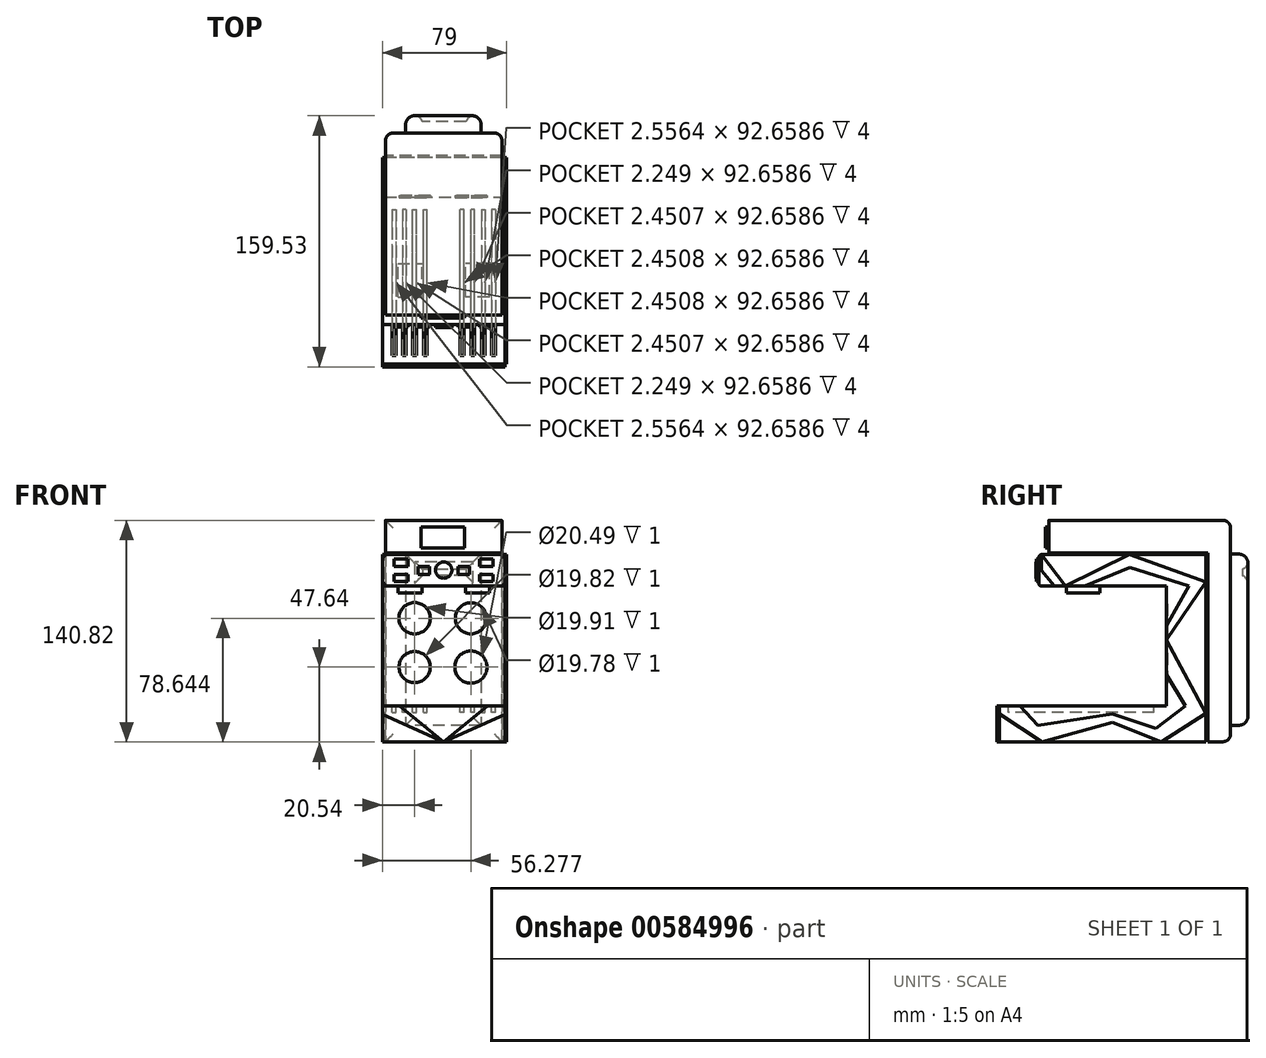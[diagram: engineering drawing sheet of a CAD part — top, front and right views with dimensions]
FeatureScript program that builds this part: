
annotation { "Feature Type Name" : "Feature", "Feature Type Description" : "" }
export const myFeature = defineFeature(function(context is Context, id is Id, definition is map)
    precondition{}
    {
        {
            var Q0;
            Q0=qCreatedBy(makeId("Right.planeOp"),FACE);
            var sketch = newSketch(context, id + "F0", { "sketchPlane" : qUnion([Q0])});
            skLineSegment(sketch, "E0", {"start": v(-54.68, 43.8) * mm, "end": v(-54.68, 23.88) * mm});
            skLineSegment(sketch, "E1", {"start": v(-54.68, 23.88) * mm, "end": v(27.35, 23.88) * mm});
            skLineSegment(sketch, "E2", {"start": v(27.35, 23.88) * mm, "end": v(27.35, -53.5) * mm});
            skLineSegment(sketch, "E3", {"start": v(27.35, -53.5) * mm, "end": v(-73.32, -53.5) * mm});
            skLineSegment(sketch, "E4", {"start": v(-73.32, -53.5) * mm, "end": v(-73.32, -74.72) * mm});
            skLineSegment(sketch, "E5", {"start": v(-73.32, -74.72) * mm, "end": v(48.83, -74.72) * mm});
            skLineSegment(sketch, "E6", {"start": v(48.83, -74.72) * mm, "end": v(48.83, 43.8) * mm});
            skLineSegment(sketch, "E7", {"start": v(48.83, 43.8) * mm, "end": v(-54.68, 43.8) * mm});
            skLineSegment(sketch, "E8", {"start": v(-46.66, 43.8) * mm, "end": v(-46.66, 64.76) * mm});
            skLineSegment(sketch, "E9", {"start": v(-46.66, 64.76) * mm, "end": v(69.53, 64.76) * mm});
            skLineSegment(sketch, "E10", {"start": v(69.53, 64.76) * mm, "end": v(69.53, -74.72) * mm});
            skLineSegment(sketch, "E11", {"start": v(48.83, -74.72) * mm, "end": v(69.53, -74.72) * mm});
            skPoint(sketch, "E12.orphan", {"position": v(69.53, -76.01) * mm});
            skSolve(sketch);
        }
        {
            var Q0;
            {var subQ0=sQuery(id+"F0.wireOp",EDGE,"E0");Q0=makeQuery(id+"F0.imprint","IMPRINT",FACE,{"disambiguationData":[TD([[makeQuery(id+"F0.imprint","IMPRINT",EDGE,{"derivedFrom":subQ0}),1.0]])]});}
            var Q1;
            {var subQ2=sQuery(id+"F0.wireOp",EDGE,"E6");Q1=makeQuery(id+"F0.imprint","IMPRINT",FACE,{"disambiguationData":[TD([[makeQuery(id+"F0.imprint","IMPRINT",EDGE,{"derivedFrom":subQ2}),-1.0]])]});}
            extrude(context, id + "F1", {"entities" : qUnion([Q0, Q1]), "depth" : 82 * mm, "offsetDistance" : 25 * mm, "symmetric" : true});
        }
        {
            var Q0;
            Q0=makeQuery(id+"F1.opExtrude","CAP_FACE",FACE,{"disambiguationData":[OSD([sQuery(id+"F0.wireOp",EDGE,"E0"),sQuery(id+"F0.wireOp",EDGE,"E1"),sQuery(id+"F0.wireOp",EDGE,"E2"),sQuery(id+"F0.wireOp",EDGE,"E3"),sQuery(id+"F0.wireOp",EDGE,"E4"),sQuery(id+"F0.wireOp",EDGE,"E5"),sQuery(id+"F0.wireOp",EDGE,"E7"),sQuery(id+"F0.wireOp",EDGE,"E8"),sQuery(id+"F0.wireOp",EDGE,"E9"),sQuery(id+"F0.wireOp",EDGE,"E10"),sQuery(id+"F0.wireOp",EDGE,"E11")])],"isStart":false});
            extrude(context, id + "F2", {"entities" : qUnion([Q0]), "operationType" : NewBodyOperationType.ADD, "depth" : 15 * mm, "offsetDistance" : 25 * mm});
        }
        {
            var Q0;
            Q0=makeQuery(id+"F1.opExtrude","SWEPT_BODY",BODY,{"disambiguationData":[OSD([sQuery(id+"F0.wireOp",EDGE,"E0"),sQuery(id+"F0.wireOp",EDGE,"E1"),sQuery(id+"F0.wireOp",EDGE,"E2"),sQuery(id+"F0.wireOp",EDGE,"E3"),sQuery(id+"F0.wireOp",EDGE,"E4"),sQuery(id+"F0.wireOp",EDGE,"E5"),sQuery(id+"F0.wireOp",EDGE,"E7"),sQuery(id+"F0.wireOp",EDGE,"E8"),sQuery(id+"F0.wireOp",EDGE,"E9"),sQuery(id+"F0.wireOp",EDGE,"E10"),sQuery(id+"F0.wireOp",EDGE,"E11")])]});
            deleteBodies(context, id + "F3", {"entities" : qUnion([Q0])});
        }
        {
            var Q0;
            Q0=qCreatedBy(makeId("Right.planeOp"),FACE);
            var sketch = newSketch(context, id + "F4", { "sketchPlane" : qUnion([Q0])});
            skLineSegment(sketch, "E13", {"start": v(-46.6, 54.07) * mm, "end": v(-46.6, 34.04) * mm});
            skLineSegment(sketch, "E14", {"start": v(-46.6, 34.04) * mm, "end": v(34.23, 34.04) * mm});
            skLineSegment(sketch, "E15", {"start": v(34.23, 34.04) * mm, "end": v(34.23, -42.06) * mm});
            skLineSegment(sketch, "E16", {"start": v(34.23, -42.06) * mm, "end": v(-71.74, -42.06) * mm});
            skLineSegment(sketch, "E17", {"start": v(-71.74, -42.06) * mm, "end": v(-71.74, -65) * mm});
            skLineSegment(sketch, "E18", {"start": v(-71.74, -65) * mm, "end": v(59.35, -65) * mm});
            skLineSegment(sketch, "E19", {"start": v(59.35, -65) * mm, "end": v(59.35, 54.07) * mm});
            skLineSegment(sketch, "E20", {"start": v(59.35, 54.07) * mm, "end": v(-46.6, 54.07) * mm});
            skSolve(sketch);
        }
        {
            var Q0;
            Q0=makeQuery(id+"F4.imprint","IMPRINT",FACE,{"disambiguationData":[TD([[makeQuery(id+"F4.imprint","IMPRINT",EDGE,{"derivedFrom":sQuery(id+"F4.wireOp",EDGE,"E13")}),1.0]])]});
            extrude(context, id + "F5", {"entities" : qUnion([Q0]), "depth" : 78 * mm, "offsetDistance" : 25 * mm, "symmetric" : true});
        }
        {
            var Q0;
            Q0=qCreatedBy(makeId("Right.planeOp"),FACE);
            var sketch = newSketch(context, id + "F6", { "sketchPlane" : qUnion([Q0])});
            skLineSegment(sketch, "E21", {"start": v(-40.38, 55.14) * mm, "end": v(60.81, 55.14) * mm});
            skLineSegment(sketch, "E22", {"start": v(60.81, 55.14) * mm, "end": v(60.81, -64.77) * mm});
            skLineSegment(sketch, "E23", {"start": v(60.81, -64.77) * mm, "end": v(75.1, -64.77) * mm});
            skLineSegment(sketch, "E24", {"start": v(75.1, -64.77) * mm, "end": v(75.1, 75.82) * mm});
            skLineSegment(sketch, "E25", {"start": v(75.1, 75.82) * mm, "end": v(-40.38, 75.82) * mm});
            skLineSegment(sketch, "E26", {"start": v(-40.38, 75.82) * mm, "end": v(-40.38, 55.14) * mm});
            skSolve(sketch);
        }
        {
            var Q0;
            Q0=makeQuery(id+"F6.imprint","IMPRINT",FACE,{"disambiguationData":[TD([[makeQuery(id+"F6.imprint","IMPRINT",EDGE,{"derivedFrom":sQuery(id+"F6.wireOp",EDGE,"E21")}),1.0]])]});
            extrude(context, id + "F7", {"entities" : qUnion([Q0]), "depth" : 74 * mm, "offsetDistance" : 25 * mm, "symmetric" : true});
        }
        {
            var Q0;
            Q0=makeQuery(id+"F5.opExtrude","SWEPT_FACE",FACE,{"disambiguationData":[OSD([sQuery(id+"F4.wireOp",EDGE,"E16")])]});
            var sketch = newSketch(context, id + "F8", { "sketchPlane" : qUnion([Q0])});
            skLineSegment(sketch, "E27.bottom", {"start": v(-32.9, 26.57) * mm, "end": v(-30.35, 26.57) * mm});
            skLineSegment(sketch, "E27.top", {"start": v(-32.9, -66.09) * mm, "end": v(-30.35, -66.09) * mm});
            skLineSegment(sketch, "E27.left", {"start": v(-32.9, 26.57) * mm, "end": v(-32.9, -66.09) * mm});
            skLineSegment(sketch, "E27.right", {"start": v(-30.35, 26.57) * mm, "end": v(-30.35, -66.09) * mm});
            skLineSegment(sketch, "E28.bottom", {"start": v(-23.97, 26.57) * mm, "end": v(-26.22, 26.57) * mm});
            skLineSegment(sketch, "E28.top", {"start": v(-23.97, -66.09) * mm, "end": v(-26.22, -66.09) * mm});
            skLineSegment(sketch, "E28.left", {"start": v(-23.97, 26.57) * mm, "end": v(-23.97, -66.09) * mm});
            skLineSegment(sketch, "E28.right", {"start": v(-26.22, 26.57) * mm, "end": v(-26.22, -66.09) * mm});
            skLineSegment(sketch, "E29.bottom", {"start": v(-19.69, -66.09) * mm, "end": v(-17.24, -66.09) * mm});
            skLineSegment(sketch, "E29.top", {"start": v(-19.69, 26.57) * mm, "end": v(-17.24, 26.57) * mm});
            skLineSegment(sketch, "E29.left", {"start": v(-19.69, -66.09) * mm, "end": v(-19.69, 26.57) * mm});
            skLineSegment(sketch, "E29.right", {"start": v(-17.24, -66.09) * mm, "end": v(-17.24, 26.57) * mm});
            skLineSegment(sketch, "E30.bottom", {"start": v(-12.9, -66.09) * mm, "end": v(-10.45, -66.09) * mm});
            skLineSegment(sketch, "E30.top", {"start": v(-12.9, 26.57) * mm, "end": v(-10.45, 26.57) * mm});
            skLineSegment(sketch, "E30.left", {"start": v(-12.9, -66.09) * mm, "end": v(-12.9, 26.57) * mm});
            skLineSegment(sketch, "E30.right", {"start": v(-10.45, -66.09) * mm, "end": v(-10.45, 26.57) * mm});
            skLineSegment(sketch, "E31.MirrorCS", {"start": v(12.9, -66.09) * mm, "end": v(12.9, 26.57) * mm});
            skLineSegment(sketch, "E32.MirrorCS", {"start": v(10.45, -66.09) * mm, "end": v(10.45, 26.57) * mm});
            skLineSegment(sketch, "E33.MirrorCS", {"start": v(17.24, -66.09) * mm, "end": v(17.24, 26.57) * mm});
            skLineSegment(sketch, "E34.MirrorCS", {"start": v(19.69, -66.09) * mm, "end": v(19.69, 26.57) * mm});
            skLineSegment(sketch, "E35.MirrorCS", {"start": v(26.22, 26.57) * mm, "end": v(26.22, -66.09) * mm});
            skLineSegment(sketch, "E36.MirrorCS", {"start": v(23.97, 26.57) * mm, "end": v(23.97, -66.09) * mm});
            skLineSegment(sketch, "E37.MirrorCS", {"start": v(32.9, 26.57) * mm, "end": v(32.9, -66.09) * mm});
            skLineSegment(sketch, "E38.MirrorCS", {"start": v(30.35, 26.57) * mm, "end": v(30.35, -66.09) * mm});
            skLineSegment(sketch, "E39.MirrorCS", {"start": v(32.9, 26.57) * mm, "end": v(30.35, 26.57) * mm});
            skLineSegment(sketch, "E40.MirrorCS", {"start": v(23.97, 26.57) * mm, "end": v(26.22, 26.57) * mm});
            skLineSegment(sketch, "E41.MirrorCS", {"start": v(19.69, 26.57) * mm, "end": v(17.24, 26.57) * mm});
            skLineSegment(sketch, "E42.MirrorCS", {"start": v(12.9, 26.57) * mm, "end": v(10.45, 26.57) * mm});
            skLineSegment(sketch, "E43.MirrorCS", {"start": v(32.9, -66.09) * mm, "end": v(30.35, -66.09) * mm});
            skLineSegment(sketch, "E44.MirrorCS", {"start": v(23.97, -66.09) * mm, "end": v(26.22, -66.09) * mm});
            skLineSegment(sketch, "E45.MirrorCS", {"start": v(19.69, -66.09) * mm, "end": v(17.24, -66.09) * mm});
            skLineSegment(sketch, "E46.MirrorCS", {"start": v(12.9, -66.09) * mm, "end": v(10.45, -66.09) * mm});
            skSolve(sketch);
        }
        {
            var Q0;
            Q0=makeQuery(id+"F8.imprint","IMPRINT",FACE,{"disambiguationData":[TD([[makeQuery(id+"F8.imprint","IMPRINT",EDGE,{"derivedFrom":sQuery(id+"F8.wireOp",EDGE,"E27.bottom")}),-1.0]])]});
            var Q1;
            Q1=makeQuery(id+"F8.imprint","IMPRINT",FACE,{"disambiguationData":[TD([[makeQuery(id+"F8.imprint","IMPRINT",EDGE,{"derivedFrom":sQuery(id+"F8.wireOp",EDGE,"E28.bottom")}),1.0]])]});
            var Q2;
            Q2=makeQuery(id+"F8.imprint","IMPRINT",FACE,{"disambiguationData":[TD([[makeQuery(id+"F8.imprint","IMPRINT",EDGE,{"derivedFrom":sQuery(id+"F8.wireOp",EDGE,"E29.bottom")}),1.0]])]});
            var Q3;
            Q3=makeQuery(id+"F8.imprint","IMPRINT",FACE,{"disambiguationData":[TD([[makeQuery(id+"F8.imprint","IMPRINT",EDGE,{"derivedFrom":sQuery(id+"F8.wireOp",EDGE,"E30.bottom")}),1.0]])]});
            var Q4;
            Q4=makeQuery(id+"F8.imprint","IMPRINT",FACE,{"disambiguationData":[TD([[makeQuery(id+"F8.imprint","IMPRINT",EDGE,{"derivedFrom":sQuery(id+"F8.wireOp",EDGE,"E31.MirrorCS")}),1.0]])]});
            var Q5;
            Q5=makeQuery(id+"F8.imprint","IMPRINT",FACE,{"disambiguationData":[TD([[makeQuery(id+"F8.imprint","IMPRINT",EDGE,{"derivedFrom":sQuery(id+"F8.wireOp",EDGE,"E33.MirrorCS")}),-1.0]])]});
            var Q6;
            Q6=makeQuery(id+"F8.imprint","IMPRINT",FACE,{"disambiguationData":[TD([[makeQuery(id+"F8.imprint","IMPRINT",EDGE,{"derivedFrom":sQuery(id+"F8.wireOp",EDGE,"E35.MirrorCS")}),-1.0]])]});
            var Q7;
            Q7=makeQuery(id+"F8.imprint","IMPRINT",FACE,{"disambiguationData":[TD([[makeQuery(id+"F8.imprint","IMPRINT",EDGE,{"derivedFrom":sQuery(id+"F8.wireOp",EDGE,"E37.MirrorCS")}),-1.0]])]});
            extrude(context, id + "F9", {"entities" : qUnion([Q0, Q1, Q2, Q3, Q4, Q5, Q6, Q7]), "operationType" : NewBodyOperationType.REMOVE, "oppositeDirection" : true, "depth" : 4 * mm, "offsetDistance" : 25 * mm});
        }
        {
            var Q0;
            Q0=makeQuery(id+"F5.opExtrude","SWEPT_FACE",FACE,{"disambiguationData":[OSD([sQuery(id+"F4.wireOp",EDGE,"E14")])]});
            var sketch = newSketch(context, id + "F10", { "sketchPlane" : qUnion([Q0])});
            skLineSegment(sketch, "E47.bottom", {"start": v(-29.04, 29.07) * mm, "end": v(-13.9, 29.07) * mm});
            skLineSegment(sketch, "E47.top", {"start": v(-29.04, 7.88) * mm, "end": v(-13.9, 7.88) * mm});
            skLineSegment(sketch, "E47.left", {"start": v(-29.04, 29.07) * mm, "end": v(-29.04, 7.88) * mm});
            skLineSegment(sketch, "E47.right", {"start": v(-13.9, 29.07) * mm, "end": v(-13.9, 7.88) * mm});
            skLineSegment(sketch, "E48.MirrorCS", {"start": v(13.9, 29.07) * mm, "end": v(13.9, 7.88) * mm});
            skLineSegment(sketch, "E49.MirrorCS", {"start": v(29.04, 29.07) * mm, "end": v(13.9, 29.07) * mm});
            skLineSegment(sketch, "E50.MirrorCS", {"start": v(29.04, 29.07) * mm, "end": v(29.04, 7.88) * mm});
            skLineSegment(sketch, "E51.MirrorCS", {"start": v(29.04, 7.88) * mm, "end": v(13.9, 7.88) * mm});
            skSolve(sketch);
        }
        {
            var Q0;
            Q0=makeQuery(id+"F10.imprint","IMPRINT",FACE,{"disambiguationData":[TD([[makeQuery(id+"F10.imprint","IMPRINT",EDGE,{"derivedFrom":sQuery(id+"F10.wireOp",EDGE,"E47.bottom")}),-1.0]])]});
            var Q1;
            Q1=makeQuery(id+"F10.imprint","IMPRINT",FACE,{"disambiguationData":[TD([[makeQuery(id+"F10.imprint","IMPRINT",EDGE,{"derivedFrom":sQuery(id+"F10.wireOp",EDGE,"E48.MirrorCS")}),1.0]])]});
            extrude(context, id + "F11", {"entities" : qUnion([Q0, Q1]), "depth" : 4.2 * mm, "offsetDistance" : 25 * mm});
        }
        {
            var Q0;
            Q0=makeQuery(id+"F7.opExtrude","SWEPT_FACE",FACE,{"disambiguationData":[OSD([sQuery(id+"F6.wireOp",EDGE,"E26")])]});
            var sketch = newSketch(context, id + "F12", { "sketchPlane" : qUnion([Q0])});
            skLineSegment(sketch, "E52.bottom", {"start": v(-14.42, 71.67) * mm, "end": v(13.24, 71.67) * mm});
            skLineSegment(sketch, "E52.top", {"start": v(-14.42, 58.43) * mm, "end": v(13.24, 58.43) * mm});
            skLineSegment(sketch, "E52.left", {"start": v(-14.42, 71.67) * mm, "end": v(-14.42, 58.43) * mm});
            skLineSegment(sketch, "E52.right", {"start": v(13.24, 71.67) * mm, "end": v(13.24, 58.43) * mm});
            skSolve(sketch);
        }
        {
            var Q0;
            Q0=makeQuery(id+"F12.imprint","IMPRINT",FACE,{"disambiguationData":[TD([[makeQuery(id+"F12.imprint","IMPRINT",EDGE,{"derivedFrom":sQuery(id+"F12.wireOp",EDGE,"E52.bottom")}),-1.0]])]});
            extrude(context, id + "F13", {"entities" : qUnion([Q0]), "depth" : 2 * mm, "offsetDistance" : 25 * mm});
        }
        {
            var Q0;
            Q0=makeQuery(id+"F5.opExtrude","SWEPT_FACE",FACE,{"disambiguationData":[OSD([sQuery(id+"F4.wireOp",EDGE,"E13")])]});
            var sketch = newSketch(context, id + "F14", { "sketchPlane" : qUnion([Q0])});
            skLineSegment(sketch, "E53.bottom", {"start": v(-31.44, 51.34) * mm, "end": v(-22.7, 51.34) * mm});
            skLineSegment(sketch, "E53.top", {"start": v(-31.44, 46.62) * mm, "end": v(-22.7, 46.62) * mm});
            skLineSegment(sketch, "E53.left", {"start": v(-31.44, 51.34) * mm, "end": v(-31.44, 46.62) * mm});
            skLineSegment(sketch, "E53.right", {"start": v(-22.7, 51.34) * mm, "end": v(-22.7, 46.62) * mm});
            skLineSegment(sketch, "E54.bottom", {"start": v(-31.44, 41.42) * mm, "end": v(-22.7, 41.42) * mm});
            skLineSegment(sketch, "E54.top", {"start": v(-31.44, 37.16) * mm, "end": v(-22.7, 37.16) * mm});
            skLineSegment(sketch, "E54.left", {"start": v(-31.44, 41.42) * mm, "end": v(-31.44, 37.16) * mm});
            skLineSegment(sketch, "E54.right", {"start": v(-22.7, 41.42) * mm, "end": v(-22.7, 37.16) * mm});
            skLineSegment(sketch, "E55.bottom", {"start": v(-16.3, 46.62) * mm, "end": v(-8.98, 46.62) * mm});
            skLineSegment(sketch, "E55.top", {"start": v(-16.3, 41.42) * mm, "end": v(-8.98, 41.42) * mm});
            skLineSegment(sketch, "E55.left", {"start": v(-16.3, 46.62) * mm, "end": v(-16.3, 41.42) * mm});
            skLineSegment(sketch, "E55.right", {"start": v(-8.98, 46.62) * mm, "end": v(-8.98, 41.42) * mm});
            skLineSegment(sketch, "E56.MirrorCS", {"start": v(8.98, 46.62) * mm, "end": v(8.98, 41.42) * mm});
            skLineSegment(sketch, "E57.MirrorCS", {"start": v(16.3, 46.62) * mm, "end": v(16.3, 41.42) * mm});
            skLineSegment(sketch, "E58.MirrorCS", {"start": v(16.3, 41.42) * mm, "end": v(8.98, 41.42) * mm});
            skLineSegment(sketch, "E59.MirrorCS", {"start": v(16.3, 46.62) * mm, "end": v(8.98, 46.62) * mm});
            skLineSegment(sketch, "E60.MirrorCS", {"start": v(31.44, 51.34) * mm, "end": v(31.44, 46.62) * mm});
            skLineSegment(sketch, "E61.MirrorCS", {"start": v(31.44, 51.34) * mm, "end": v(22.7, 51.34) * mm});
            skLineSegment(sketch, "E62.MirrorCS", {"start": v(22.7, 51.34) * mm, "end": v(22.7, 46.62) * mm});
            skLineSegment(sketch, "E63.MirrorCS", {"start": v(31.44, 46.62) * mm, "end": v(22.7, 46.62) * mm});
            skLineSegment(sketch, "E64.MirrorCS", {"start": v(31.44, 41.42) * mm, "end": v(22.7, 41.42) * mm});
            skLineSegment(sketch, "E65.MirrorCS", {"start": v(31.44, 41.42) * mm, "end": v(31.44, 37.16) * mm});
            skLineSegment(sketch, "E66.MirrorCS", {"start": v(31.44, 37.16) * mm, "end": v(22.7, 37.16) * mm});
            skLineSegment(sketch, "E67.MirrorCS", {"start": v(22.7, 41.42) * mm, "end": v(22.7, 37.16) * mm});
            skSolve(sketch);
        }
        {
            var Q0;
            Q0=makeQuery(id+"F14.imprint","IMPRINT",FACE,{"disambiguationData":[TD([[makeQuery(id+"F14.imprint","IMPRINT",EDGE,{"derivedFrom":sQuery(id+"F14.wireOp",EDGE,"E56.MirrorCS")}),1.0]])]});
            var Q1;
            Q1=makeQuery(id+"F14.imprint","IMPRINT",FACE,{"disambiguationData":[TD([[makeQuery(id+"F14.imprint","IMPRINT",EDGE,{"derivedFrom":sQuery(id+"F14.wireOp",EDGE,"E60.MirrorCS")}),-1.0]])]});
            var Q2;
            Q2=makeQuery(id+"F14.imprint","IMPRINT",FACE,{"disambiguationData":[TD([[makeQuery(id+"F14.imprint","IMPRINT",EDGE,{"derivedFrom":sQuery(id+"F14.wireOp",EDGE,"E64.MirrorCS")}),1.0]])]});
            var Q3;
            Q3=makeQuery(id+"F14.imprint","IMPRINT",FACE,{"disambiguationData":[TD([[makeQuery(id+"F14.imprint","IMPRINT",EDGE,{"derivedFrom":sQuery(id+"F14.wireOp",EDGE,"E55.bottom")}),-1.0]])]});
            var Q4;
            Q4=makeQuery(id+"F14.imprint","IMPRINT",FACE,{"disambiguationData":[TD([[makeQuery(id+"F14.imprint","IMPRINT",EDGE,{"derivedFrom":sQuery(id+"F14.wireOp",EDGE,"E54.bottom")}),-1.0]])]});
            var Q5;
            Q5=makeQuery(id+"F14.imprint","IMPRINT",FACE,{"disambiguationData":[TD([[makeQuery(id+"F14.imprint","IMPRINT",EDGE,{"derivedFrom":sQuery(id+"F14.wireOp",EDGE,"E53.bottom")}),-1.0]])]});
            extrude(context, id + "F15", {"entities" : qUnion([Q0, Q1, Q2, Q3, Q4, Q5]), "depth" : 1.5 * mm, "offsetDistance" : 25 * mm});
        }
        {
            var Q0;
            Q0=makeQuery(id+"F5.opExtrude","SWEPT_FACE",FACE,{"disambiguationData":[OSD([sQuery(id+"F4.wireOp",EDGE,"E13")])]});
            var sketch = newSketch(context, id + "F16", { "sketchPlane" : qUnion([Q0])});
            skCircle(sketch, "E68", {"center": v(0, 44.25) * mm, "radius": 5.19 * mm});
            skSolve(sketch);
        }
        {
            var Q0;
            Q0=makeQuery(id+"F16.imprint","IMPRINT",FACE,{"disambiguationData":[TD([[makeQuery(id+"F16.imprint","IMPRINT",EDGE,{"derivedFrom":sQuery(id+"F16.wireOp",EDGE,"E68")}),1.0]])]});
            extrude(context, id + "F17", {"entities" : qUnion([Q0]), "depth" : 1.9 * mm, "offsetDistance" : 25 * mm});
        }
        {
            var Q0;
            Q0=makeQuery(id+"F7.opExtrude","SWEPT_FACE",FACE,{"disambiguationData":[OSD([sQuery(id+"F6.wireOp",EDGE,"E24")])]});
            var sketch = newSketch(context, id + "F18", { "sketchPlane" : qUnion([Q0])});
            skLineSegment(sketch, "E69.bottom", {"start": v(-23.67, 54.35) * mm, "end": v(24.14, 54.35) * mm});
            skLineSegment(sketch, "E69.top", {"start": v(-23.67, -54.28) * mm, "end": v(24.14, -54.28) * mm});
            skLineSegment(sketch, "E69.left", {"start": v(-23.67, 54.35) * mm, "end": v(-23.67, -54.28) * mm});
            skLineSegment(sketch, "E69.right", {"start": v(24.14, 54.35) * mm, "end": v(24.14, -54.28) * mm});
            skSolve(sketch);
        }
        {
            var Q0;
            Q0=makeQuery(id+"F18.imprint","IMPRINT",FACE,{"disambiguationData":[TD([[makeQuery(id+"F18.imprint","IMPRINT",EDGE,{"derivedFrom":sQuery(id+"F18.wireOp",EDGE,"E69.bottom")}),-1.0]])]});
            extrude(context, id + "F19", {"entities" : qUnion([Q0]), "depth" : 11 * mm, "offsetDistance" : 25 * mm});
        }
        {
            var Q0;
            Q0=makeQuery(id+"F19.opExtrude","CAP_FACE",FACE,{"disambiguationData":[OSD([sQuery(id+"F18.wireOp",EDGE,"E69.bottom"),sQuery(id+"F18.wireOp",EDGE,"E69.top"),sQuery(id+"F18.wireOp",EDGE,"E69.left"),sQuery(id+"F18.wireOp",EDGE,"E69.right")])],"isStart":false});
            var sketch = newSketch(context, id + "F20", { "sketchPlane" : qUnion([Q0])});
            skLineSegment(sketch, "E70.bottom", {"start": v(-14.2, 44.65) * mm, "end": v(13.5, 44.65) * mm});
            skLineSegment(sketch, "E70.top", {"start": v(-14.2, 40.86) * mm, "end": v(13.5, 40.86) * mm});
            skLineSegment(sketch, "E70.left", {"start": v(-14.2, 44.65) * mm, "end": v(-14.2, 40.86) * mm});
            skLineSegment(sketch, "E70.right", {"start": v(13.5, 44.65) * mm, "end": v(13.5, 40.86) * mm});
            skSolve(sketch);
        }
        {
            var Q0;
            Q0=makeQuery(id+"F20.imprint","IMPRINT",FACE,{"disambiguationData":[TD([[makeQuery(id+"F20.imprint","IMPRINT",EDGE,{"derivedFrom":sQuery(id+"F20.wireOp",EDGE,"E70.bottom")}),-1.0]])]});
            extrude(context, id + "F21", {"entities" : qUnion([Q0]), "operationType" : NewBodyOperationType.REMOVE, "oppositeDirection" : true, "depth" : 3.6 * mm, "offsetDistance" : 25 * mm});
        }
        {
            var Q0;
            Q0=makeQuery(id+"F5.opExtrude","SWEPT_FACE",FACE,{"disambiguationData":[OSD([sQuery(id+"F4.wireOp",EDGE,"E15")])]});
            var sketch = newSketch(context, id + "F22", { "sketchPlane" : qUnion([Q0])});
            skCircle(sketch, "E71", {"center": v(-18.46, 13.64) * mm, "radius": 9.95 * mm});
            skCircle(sketch, "E72", {"center": v(17.28, 13.64) * mm, "radius": 9.89 * mm});
            skCircle(sketch, "E73", {"center": v(-18.46, -17.36) * mm, "radius": 9.91 * mm});
            skCircle(sketch, "E74", {"center": v(17.28, -17.36) * mm, "radius": 10.24 * mm});
            skSolve(sketch);
        }
        {
            var Q0;
            Q0=makeQuery(id+"F7.opExtrude","SWEPT_FACE",FACE,{"disambiguationData":[OSD([sQuery(id+"F6.wireOp",EDGE,"E24")])]});
            fillet(context, id + "F23", {"entities" : qUnion([Q0]), "radius" : 4.83 * mm, "tangentPropagation" : true, "allowEdgeOverflow" : false});
        }
        {
            var Q0;
            Q0=makeQuery(id+"F7.opExtrude","SWEPT_FACE",FACE,{"disambiguationData":[OSD([sQuery(id+"F6.wireOp",EDGE,"E25")])]});
            fillet(context, id + "F24", {"entities" : qUnion([Q0]), "radius" : 0.02 * mm, "tangentPropagation" : true, "allowEdgeOverflow" : false});
        }
        {
            var Q0;
            Q0=makeQuery(id+"F5.opExtrude","SWEPT_FACE",FACE,{"disambiguationData":[OSD([sQuery(id+"F4.wireOp",EDGE,"E13")])]});
            fillet(context, id + "F25", {"entities" : qUnion([Q0]), "radius" : 1.69 * mm, "tangentPropagation" : true, "allowEdgeOverflow" : false});
        }
        {
            var Q0;
            Q0=makeQuery(id+"F5.opExtrude","SWEPT_FACE",FACE,{"disambiguationData":[OSD([sQuery(id+"F4.wireOp",EDGE,"E17")])]});
            var sketch = newSketch(context, id + "F26", { "sketchPlane" : qUnion([Q0])});
            skLineSegment(sketch, "E75", {"start": v(-39, -47.42) * mm, "end": v(0, -65) * mm});
            skLineSegment(sketch, "E76", {"start": v(0, -65) * mm, "end": v(-27.93, -42.06) * mm});
            skLineSegment(sketch, "E77", {"start": v(-27.93, -42.06) * mm, "end": v(-39, -42.06) * mm});
            skLineSegment(sketch, "E78", {"start": v(-39, -42.06) * mm, "end": v(-39, -47.42) * mm});
            skLineSegment(sketch, "E79.MirrorCS", {"start": v(0, -65) * mm, "end": v(27.93, -42.06) * mm});
            skLineSegment(sketch, "E80.MirrorCS", {"start": v(39, -47.42) * mm, "end": v(0, -65) * mm});
            skLineSegment(sketch, "E81.MirrorCS", {"start": v(27.93, -42.06) * mm, "end": v(39, -42.06) * mm});
            skLineSegment(sketch, "E82.MirrorCS", {"start": v(39, -42.06) * mm, "end": v(39, -47.42) * mm});
            skSolve(sketch);
        }
        {
            var Q0;
            Q0=makeQuery(id+"F26.imprint","IMPRINT",FACE,{"disambiguationData":[TD([[makeQuery(id+"F26.imprint","IMPRINT",EDGE,{"derivedFrom":sQuery(id+"F26.wireOp",EDGE,"E79.MirrorCS")}),-1.0]])]});
            var Q1;
            Q1=makeQuery(id+"F26.imprint","IMPRINT",FACE,{"disambiguationData":[TD([[makeQuery(id+"F26.imprint","IMPRINT",EDGE,{"derivedFrom":sQuery(id+"F26.wireOp",EDGE,"E75")}),1.0]])]});
            extrude(context, id + "F27", {"entities" : qUnion([Q0, Q1]), "depth" : 1.7 * mm, "offsetDistance" : 25 * mm});
        }
        {
            var Q0;
            Q0=makeQuery(id+"F19.opExtrude","CAP_FACE",FACE,{"disambiguationData":[OSD([sQuery(id+"F18.wireOp",EDGE,"E69.bottom"),sQuery(id+"F18.wireOp",EDGE,"E69.top"),sQuery(id+"F18.wireOp",EDGE,"E69.left"),sQuery(id+"F18.wireOp",EDGE,"E69.right")])],"isStart":false});
            fillet(context, id + "F28", {"entities" : qUnion([Q0]), "radius" : 5.55 * mm, "tangentPropagation" : true, "allowEdgeOverflow" : false});
        }
        {
            var Q0;
            Q0=makeQuery(id+"F5.opExtrude","CAP_FACE",FACE,{"disambiguationData":[OSD([sQuery(id+"F4.wireOp",EDGE,"E13"),sQuery(id+"F4.wireOp",EDGE,"E14"),sQuery(id+"F4.wireOp",EDGE,"E15"),sQuery(id+"F4.wireOp",EDGE,"E16"),sQuery(id+"F4.wireOp",EDGE,"E17"),sQuery(id+"F4.wireOp",EDGE,"E18"),sQuery(id+"F4.wireOp",EDGE,"E19"),sQuery(id+"F4.wireOp",EDGE,"E20")])],"isStart":false});
            var sketch = newSketch(context, id + "F29", { "sketchPlane" : qUnion([Q0])});
            skLineSegment(sketch, "E83", {"start": v(-71.74, -47.18) * mm, "end": v(-44.6, -65) * mm});
            skLineSegment(sketch, "E84", {"start": v(-44.6, -65) * mm, "end": v(0, -52.62) * mm});
            skLineSegment(sketch, "E85", {"start": v(0, -52.62) * mm, "end": v(31.14, -65) * mm});
            skLineSegment(sketch, "E86", {"start": v(31.14, -65) * mm, "end": v(59.35, -46.94) * mm});
            skLineSegment(sketch, "E87", {"start": v(59.35, -46.94) * mm, "end": v(34.23, 0) * mm});
            skLineSegment(sketch, "E88", {"start": v(34.23, 0) * mm, "end": v(59.35, 36.84) * mm});
            skLineSegment(sketch, "E89", {"start": v(59.35, 36.84) * mm, "end": v(10.8, 54.07) * mm});
            skLineSegment(sketch, "E90", {"start": v(10.8, 54.07) * mm, "end": v(-29.92, 34.04) * mm});
            skLineSegment(sketch, "E91", {"start": v(-29.92, 34.04) * mm, "end": v(-44.92, 54.07) * mm});
            skLineSegment(sketch, "E92", {"start": v(-71.74, -47.18) * mm, "end": v(-71.74, -42.06) * mm});
            skLineSegment(sketch, "E93", {"start": v(-71.74, -42.06) * mm, "end": v(-58.55, -42.06) * mm});
            skLineSegment(sketch, "E94", {"start": v(-58.55, -42.06) * mm, "end": v(-47.2, -54.28) * mm});
            skLineSegment(sketch, "E95", {"start": v(-47.2, -54.28) * mm, "end": v(0, -47.18) * mm});
            skLineSegment(sketch, "E96", {"start": v(0, -47.18) * mm, "end": v(27.83, -56.41) * mm});
            skLineSegment(sketch, "E97", {"start": v(27.83, -56.41) * mm, "end": v(46.3, -42.06) * mm});
            skLineSegment(sketch, "E98", {"start": v(46.3, -42.06) * mm, "end": v(34.23, -22.1) * mm});
            skLineSegment(sketch, "E99", {"start": v(34.23, -22.1) * mm, "end": v(34.23, 0) * mm});
            skLineSegment(sketch, "E100", {"start": v(34.23, 0) * mm, "end": v(34.23, 8.91) * mm});
            skLineSegment(sketch, "E101", {"start": v(34.23, 8.91) * mm, "end": v(48.66, 34.04) * mm});
            skLineSegment(sketch, "E102", {"start": v(48.66, 34.04) * mm, "end": v(11.03, 46.07) * mm});
            skLineSegment(sketch, "E103", {"start": v(11.03, 46.07) * mm, "end": v(-17.37, 34.04) * mm});
            skLineSegment(sketch, "E104", {"start": v(-17.37, 34.04) * mm, "end": v(-36.78, 34.04) * mm});
            skLineSegment(sketch, "E105", {"start": v(-36.78, 34.04) * mm, "end": v(-44.92, 44.06) * mm});
            skLineSegment(sketch, "E106", {"start": v(-44.92, 44.06) * mm, "end": v(-44.92, 54.07) * mm});
            skSolve(sketch);
        }
        {
            var Q0;
            Q0=makeQuery(id+"F29.imprint","IMPRINT",FACE,{"disambiguationData":[TD([[makeQuery(id+"F29.imprint","IMPRINT",EDGE,{"derivedFrom":sQuery(id+"F29.wireOp",EDGE,"E83")}),1.0]])]});
            extrude(context, id + "F30", {"entities" : qUnion([Q0]), "depth" : 1 * mm, "offsetDistance" : 25 * mm});
        }
        {
            var Q0;
            Q0=makeQuery(id+"F29.imprint","IMPRINT",FACE,{"disambiguationData":[TD([[makeQuery(id+"F29.imprint","IMPRINT",EDGE,{"derivedFrom":sQuery(id+"F29.wireOp",EDGE,"E88")}),1.0]])]});
            extrude(context, id + "F31", {"entities" : qUnion([Q0]), "depth" : 1 * mm, "offsetDistance" : 25 * mm});
        }
        {
            var Q0;
            {var subQ0=sQuery(id+"F29.wireOp",EDGE,"E91");Q0=makeQuery(id+"F29.imprint","IMPRINT",FACE,{"disambiguationData":[TD([[makeQuery(id+"F29.imprint","IMPRINT",EDGE,{"derivedFrom":subQ0}),1.0]])]});}
            extrude(context, id + "F32", {"entities" : qUnion([Q0]), "depth" : 1 * mm, "offsetDistance" : 25 * mm});
        }
        {
            var Q0;
            Q0=makeQuery(id+"F22.imprint","IMPRINT",FACE,{"disambiguationData":[TD([[makeQuery(id+"F22.imprint","IMPRINT",EDGE,{"derivedFrom":sQuery(id+"F22.wireOp",EDGE,"E74")}),1.0]])]});
            var Q1;
            Q1=makeQuery(id+"F22.imprint","IMPRINT",FACE,{"disambiguationData":[TD([[makeQuery(id+"F22.imprint","IMPRINT",EDGE,{"derivedFrom":sQuery(id+"F22.wireOp",EDGE,"E73")}),1.0]])]});
            var Q2;
            Q2=makeQuery(id+"F22.imprint","IMPRINT",FACE,{"disambiguationData":[TD([[makeQuery(id+"F22.imprint","IMPRINT",EDGE,{"derivedFrom":sQuery(id+"F22.wireOp",EDGE,"E71")}),1.0]])]});
            var Q3;
            Q3=makeQuery(id+"F22.imprint","IMPRINT",FACE,{"disambiguationData":[TD([[makeQuery(id+"F22.imprint","IMPRINT",EDGE,{"derivedFrom":sQuery(id+"F22.wireOp",EDGE,"E72")}),1.0]])]});
            extrude(context, id + "F33", {"entities" : qUnion([Q0, Q1, Q2, Q3]), "operationType" : NewBodyOperationType.REMOVE, "oppositeDirection" : true, "depth" : 1 * mm, "offsetDistance" : 25 * mm});
        }
    });
